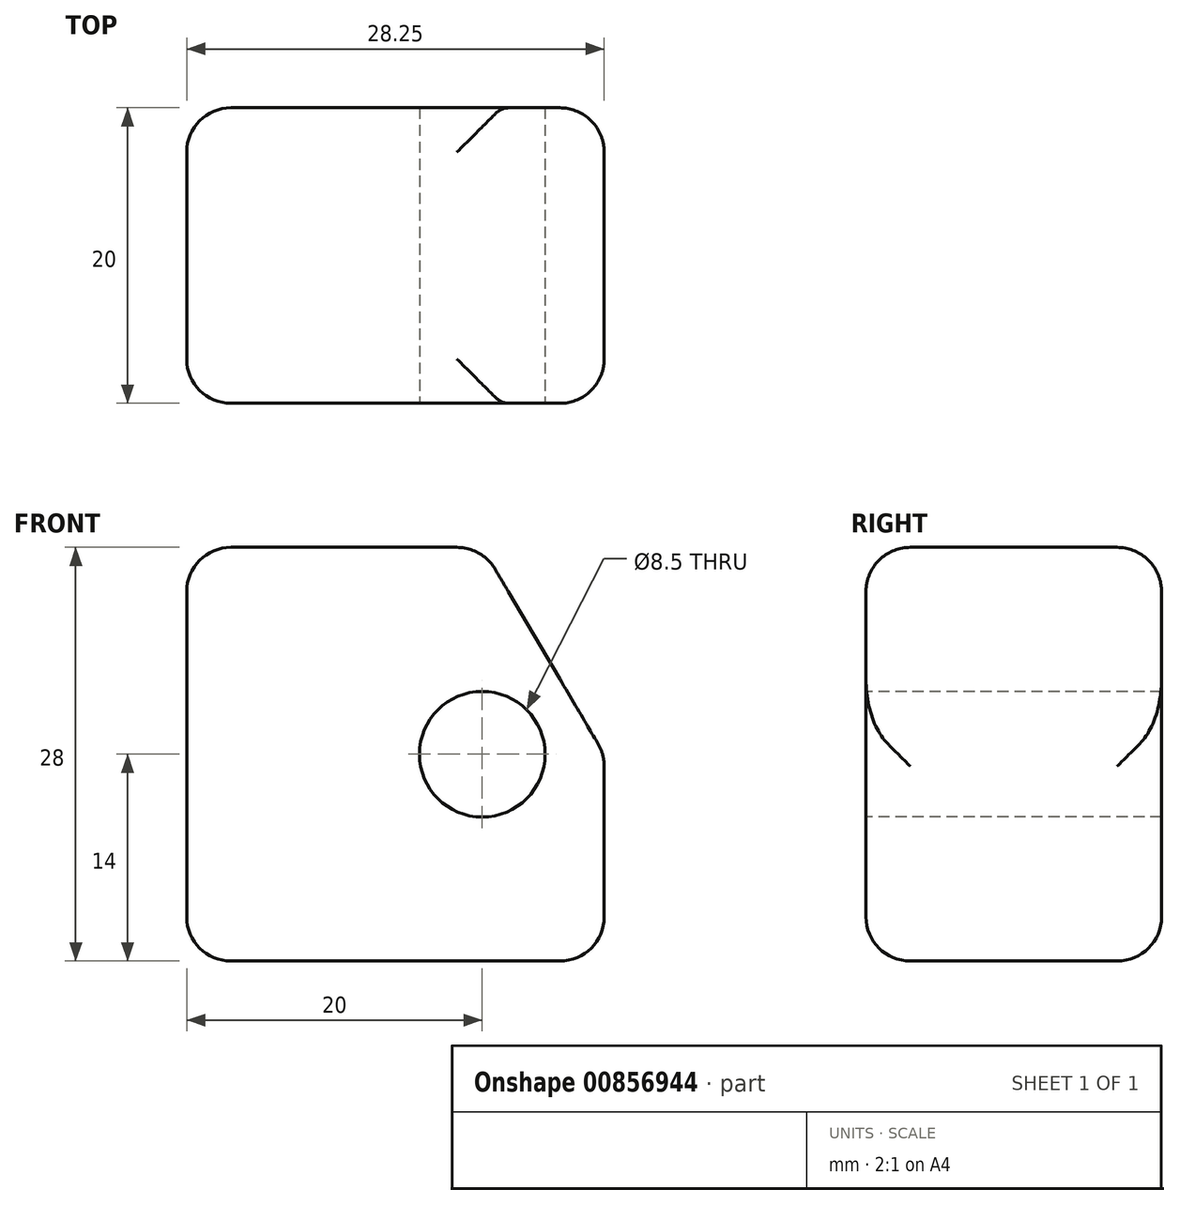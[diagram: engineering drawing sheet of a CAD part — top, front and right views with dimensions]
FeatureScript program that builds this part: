
annotation { "Feature Type Name" : "Feature", "Feature Type Description" : "" }
export const myFeature = defineFeature(function(context is Context, id is Id, definition is map)
    precondition{}
    {
        {
            var Q0;
            Q0=qCreatedBy(makeId("Front.planeOp"),FACE);
            var sketch = newSketch(context, id + "F0", { "sketchPlane" : qUnion([Q0])});
            skCircle(sketch, "E0", {"center": v(0, 0) * mm, "radius": 4.25 * mm});
            skLineSegment(sketch, "E1", {"start": v(0, 0) * mm, "end": v(0, 14) * mm});
            skLineSegment(sketch, "E2", {"start": v(0, 14) * mm, "end": v(-20, 14) * mm});
            skLineSegment(sketch, "E3", {"start": v(-20, 14) * mm, "end": v(-20, 0) * mm});
            skLineSegment(sketch, "E4", {"start": v(-20, 0) * mm, "end": v(-11.52, 0) * mm});
            skLineSegment(sketch, "E5.MirrorCS", {"start": v(-20, -14) * mm, "end": v(-20, 0) * mm});
            skLineSegment(sketch, "E6.MirrorCS", {"start": v(0, -14) * mm, "end": v(-20, -14) * mm});
            skLineSegment(sketch, "E7", {"start": v(4.25, 0) * mm, "end": v(8.25, 0) * mm});
            skLineSegment(sketch, "E8", {"start": v(0, -14) * mm, "end": v(8.25, -14) * mm});
            skLineSegment(sketch, "E9", {"start": v(8.25, -14) * mm, "end": v(8.25, 0) * mm});
            skLineSegment(sketch, "E10", {"start": v(8.25, 0) * mm, "end": v(0, 14) * mm});
            skCircle(sketch, "E11", {"center": v(0, 0) * mm, "radius": 5 * mm, "construction": true});
            skSolve(sketch);
        }
        {
            var Q0;
            Q0 = qSketchRegion(id + "F0", true);
            extrude(context, id + "F1", {"entities" : qUnion([Q0]), "oppositeDirection" : true, "depth" : 20 * mm, "offsetDistance" : 25 * mm});
        }
        {
            var Q0;
            Q0=makeQuery(id+"F1.opExtrude","SWEPT_EDGE",EDGE,{"disambiguationData":[OSD([sQuery(id+"F0.wireOp",EDGE,"E1"),sQuery(id+"F0.wireOp",EDGE,"E2"),sQuery(id+"F0.wireOp",EDGE,"E10")])]});
            var Q1;
            Q1=makeQuery(id+"F1.opExtrude","SWEPT_EDGE",EDGE,{"disambiguationData":[OSD([sQuery(id+"F0.wireOp",EDGE,"E7"),sQuery(id+"F0.wireOp",EDGE,"E9"),sQuery(id+"F0.wireOp",EDGE,"E10")])]});
            var Q2;
            Q2=makeQuery(id+"F1.opExtrude","SWEPT_EDGE",EDGE,{"disambiguationData":[OSD([sQuery(id+"F0.wireOp",EDGE,"E2"),sQuery(id+"F0.wireOp",EDGE,"E3")])]});
            var Q3;
            Q3=makeQuery(id+"F1.opExtrude","CAP_EDGE",EDGE,{"disambiguationData":[OSD([sQuery(id+"F0.wireOp",EDGE,"E3"),sQuery(id+"F0.wireOp",EDGE,"E5.MirrorCS")])],"isStart":false});
            var Q4;
            Q4=makeQuery(id+"F1.opExtrude","CAP_EDGE",EDGE,{"disambiguationData":[OSD([sQuery(id+"F0.wireOp",EDGE,"E2")])],"isStart":true});
            var Q5;
            Q5=makeQuery(id+"F1.opExtrude","CAP_EDGE",EDGE,{"disambiguationData":[OSD([sQuery(id+"F0.wireOp",EDGE,"E3"),sQuery(id+"F0.wireOp",EDGE,"E5.MirrorCS")])],"isStart":true});
            var Q6;
            Q6=makeQuery(id+"F1.opExtrude","CAP_EDGE",EDGE,{"disambiguationData":[OSD([sQuery(id+"F0.wireOp",EDGE,"E6.MirrorCS"),sQuery(id+"F0.wireOp",EDGE,"E8")])],"isStart":true});
            var Q7;
            Q7=makeQuery(id+"F1.opExtrude","CAP_EDGE",EDGE,{"disambiguationData":[OSD([sQuery(id+"F0.wireOp",EDGE,"E9")])],"isStart":true});
            var Q8;
            Q8=makeQuery(id+"F1.opExtrude","CAP_EDGE",EDGE,{"disambiguationData":[OSD([sQuery(id+"F0.wireOp",EDGE,"E2")])],"isStart":false});
            var Q9;
            Q9=makeQuery(id+"F1.opExtrude","CAP_EDGE",EDGE,{"disambiguationData":[OSD([sQuery(id+"F0.wireOp",EDGE,"E6.MirrorCS"),sQuery(id+"F0.wireOp",EDGE,"E8")])],"isStart":false});
            var Q10;
            Q10=makeQuery(id+"F1.opExtrude","SWEPT_EDGE",EDGE,{"disambiguationData":[OSD([sQuery(id+"F0.wireOp",EDGE,"E8"),sQuery(id+"F0.wireOp",EDGE,"E9")])]});
            var Q11;
            Q11=makeQuery(id+"F1.opExtrude","CAP_EDGE",EDGE,{"disambiguationData":[OSD([sQuery(id+"F0.wireOp",EDGE,"E9")])],"isStart":false});
            var Q12;
            Q12=makeQuery(id+"F1.opExtrude","SWEPT_EDGE",EDGE,{"disambiguationData":[OSD([sQuery(id+"F0.wireOp",EDGE,"E5.MirrorCS"),sQuery(id+"F0.wireOp",EDGE,"E6.MirrorCS")])]});
            fillet(context, id + "F2", {"entities" : qUnion([Q0, Q1, Q2, Q3, Q4, Q5, Q6, Q7, Q8, Q9, Q10, Q11, Q12]), "tangentPropagation" : true, "radius" : 3 * mm, "defaultsChanged" : false, "vertexSettings" : [], "allowEdgeOverflow" : false});
        }
    });
